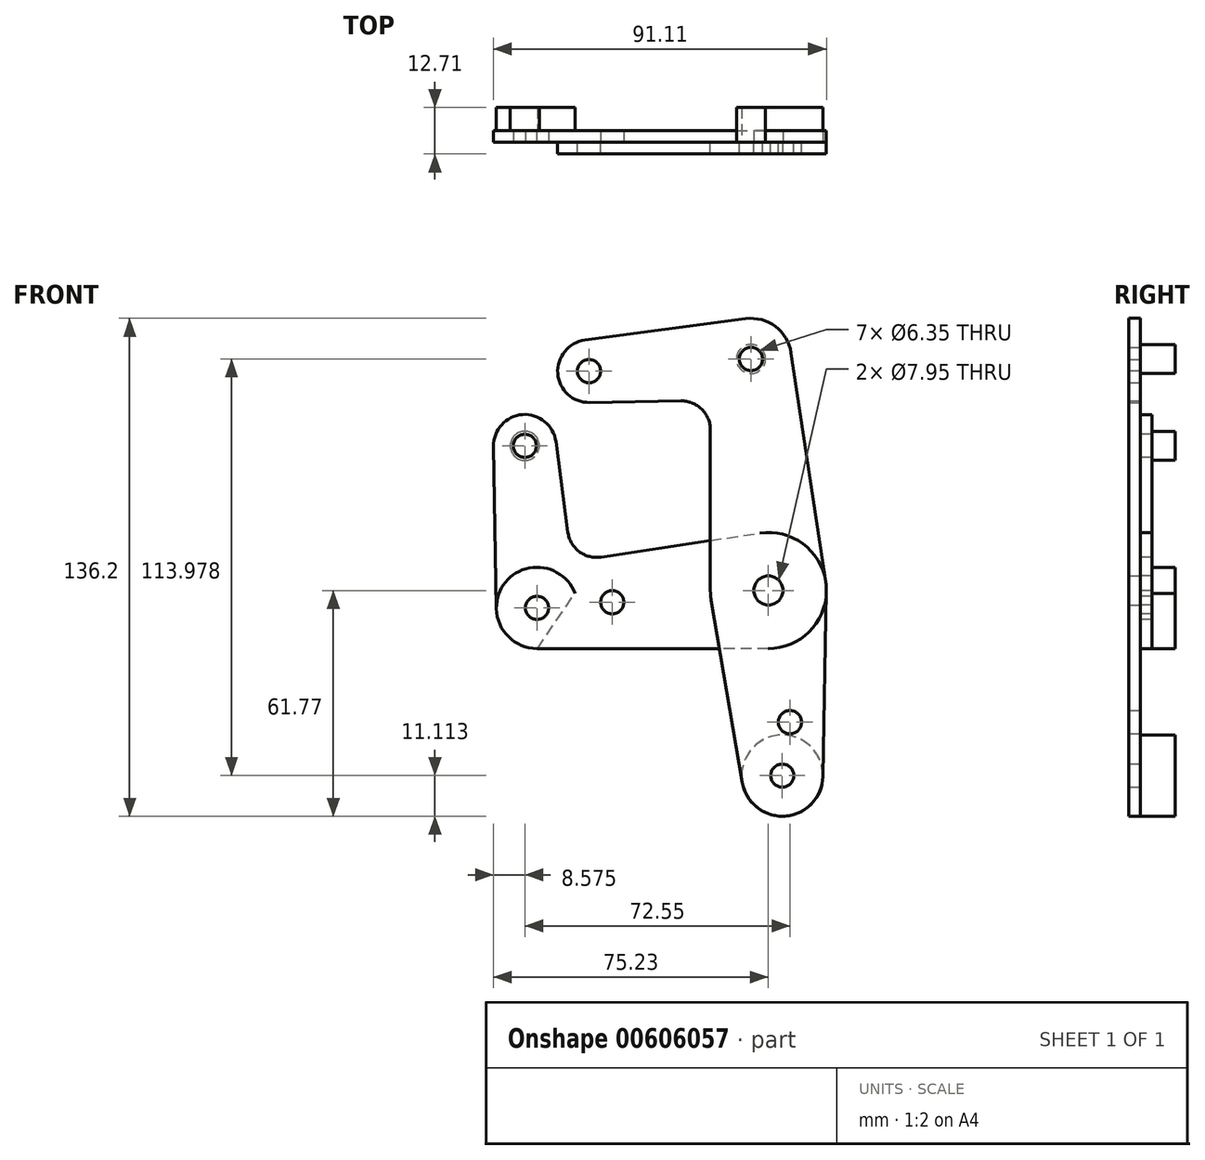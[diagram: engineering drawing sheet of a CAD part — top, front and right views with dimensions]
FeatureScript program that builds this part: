
annotation { "Feature Type Name" : "Feature", "Feature Type Description" : "" }
export const myFeature = defineFeature(function(context is Context, id is Id, definition is map)
    precondition{}
    {
        {
            var Q0;
            Q0=qCreatedBy(makeId("Front.planeOp"),FACE);
            var sketch = newSketch(context, id + "F0", { "sketchPlane" : qUnion([Q0])});
            skCircle(sketch, "E0", {"center": v(0, 0) * mm, "radius": 15.88 * mm});
            skCircle(sketch, "E1", {"center": v(0, 0) * mm, "radius": 3.98 * mm});
            skLineSegment(sketch, "E2", {"start": v(4.64, -61.74) * mm, "end": v(-4.76, 63.32) * mm, "construction": true});
            skLineSegment(sketch, "E3", {"start": v(-4.76, 63.32) * mm, "end": v(-49.09, 59.99) * mm, "construction": true});
            skCircle(sketch, "E4", {"center": v(-4.76, 63.32) * mm, "radius": 11.11 * mm});
            skCircle(sketch, "E5", {"center": v(-49.09, 59.99) * mm, "radius": 8.57 * mm});
            skCircle(sketch, "E6", {"center": v(3.81, -50.66) * mm, "radius": 11.11 * mm});
            skCircle(sketch, "E7", {"center": v(-4.76, 63.32) * mm, "radius": 3.18 * mm});
            skCircle(sketch, "E8", {"center": v(-49.09, 59.99) * mm, "radius": 3.18 * mm});
            skCircle(sketch, "E9", {"center": v(3.81, -50.66) * mm, "radius": 3.18 * mm});
            skLineSegment(sketch, "E10", {"start": v(0, 0) * mm, "end": v(-63.32, -4.76) * mm, "construction": true});
            skLineSegment(sketch, "E11", {"start": v(-63.32, -4.76) * mm, "end": v(-66.65, 39.56) * mm, "construction": true});
            skCircle(sketch, "E12", {"center": v(0, 0) * mm, "radius": 3.18 * mm});
            skLineSegment(sketch, "E13", {"start": v(6.22, 64.98) * mm, "end": v(15.7, 2.37) * mm});
            skLineSegment(sketch, "E14", {"start": v(15.87, -0.3) * mm, "end": v(14.92, -50.87) * mm});
            skLineSegment(sketch, "E15", {"start": v(-7.14, -52.53) * mm, "end": v(-15.65, -2.67) * mm});
            skLineSegment(sketch, "E16", {"start": v(-6.23, 74.34) * mm, "end": v(-50.22, 68.49) * mm});
            skCircle(sketch, "E17", {"center": v(-63.32, -4.76) * mm, "radius": 11.11 * mm});
            skCircle(sketch, "E18", {"center": v(-63.32, -4.76) * mm, "radius": 3.18 * mm});
            skCircle(sketch, "E19", {"center": v(-66.65, 39.56) * mm, "radius": 8.57 * mm});
            skCircle(sketch, "E20", {"center": v(-66.65, 39.56) * mm, "radius": 3.18 * mm});
            skCircle(sketch, "E21", {"center": v(-42.73, -3.21) * mm, "radius": 3.18 * mm});
            skCircle(sketch, "E22", {"center": v(5.9, -36.05) * mm, "radius": 3.18 * mm});
            skLineSegment(sketch, "E23", {"start": v(0, -15.88) * mm, "end": v(-63.32, -15.88) * mm});
            skLineSegment(sketch, "E24", {"start": v(-75.23, 39.4) * mm, "end": v(-74.43, -4.96) * mm});
            skLineSegment(sketch, "E25", {"start": v(-48.93, 51.42) * mm, "end": v(-23.97, 51.86) * mm});
            skLineSegment(sketch, "E26", {"start": v(-15.88, 0) * mm, "end": v(-15.87, 43.91) * mm});
            skArc(sketch, "E27.filletArc", {"start": v(-15.88, 43.91) * mm, "mid": v(-18.25, 49.59) * mm, "end": v(-23.97, 51.86) * mm});
            skLineSegment(sketch, "E28", {"start": v(5.9, -36.05) * mm, "end": v(2.75, -36.58) * mm, "construction": true});
            skLineSegment(sketch, "E29", {"start": v(-58.16, 40.7) * mm, "end": v(-54.86, 15.94) * mm});
            skLineSegment(sketch, "E30", {"start": v(-45.8, 9.13) * mm, "end": v(0, 16.06) * mm});
            skArc(sketch, "E31.filletArc", {"start": v(-54.86, 15.94) * mm, "mid": v(-51.76, 10.63) * mm, "end": v(-45.8, 9.13) * mm});
            skLineSegment(sketch, "E32", {"start": v(3.81, -50.66) * mm, "end": v(-63.32, -4.76) * mm, "construction": true});
            skSolve(sketch);
        }
        {
            var Q0;
            {var subQ0=sQuery(id+"F0.wireOp",EDGE,"E13");Q0=makeQuery(id+"F0.imprint","IMPRINT",FACE,{"disambiguationData":[TD([[makeQuery(id+"F0.imprint","IMPRINT",EDGE,{"derivedFrom":subQ0}),-1.0]])]});}
            var Q1;
            Q1=makeQuery(id+"F0.imprint","IMPRINT",FACE,{"disambiguationData":[TD([[makeQuery(id+"F0.imprint","IMPRINT",EDGE,{"derivedFrom":sQuery(id+"F0.wireOp",EDGE,"E1")}),-1.0]])]});
            var Q2;
            {var subQ0=sQuery(id+"F0.wireOp",EDGE,"E14");Q2=makeQuery(id+"F0.imprint","IMPRINT",FACE,{"disambiguationData":[TD([[makeQuery(id+"F0.imprint","IMPRINT",EDGE,{"derivedFrom":subQ0}),-1.0]])]});}
            var Q3;
            Q3=makeQuery(id+"F0.imprint","IMPRINT",FACE,{"disambiguationData":[TD([[makeQuery(id+"F0.imprint","IMPRINT",EDGE,{"derivedFrom":sQuery(id+"F0.wireOp",EDGE,"E9")}),-1.0]])]});
            var Q4;
            Q4=makeQuery(id+"F0.imprint","IMPRINT",FACE,{"disambiguationData":[TD([[makeQuery(id+"F0.imprint","IMPRINT",EDGE,{"derivedFrom":sQuery(id+"F0.wireOp",EDGE,"E7")}),-1.0]])]});
            var Q5;
            Q5=makeQuery(id+"F0.imprint","IMPRINT",FACE,{"disambiguationData":[TD([[makeQuery(id+"F0.imprint","IMPRINT",EDGE,{"derivedFrom":sQuery(id+"F0.wireOp",EDGE,"E8")}),-1.0]])]});
            var Q6;
            {var subQ0=sQuery(id+"F0.wireOp",EDGE,"E26");var subQ1=sQuery(id+"F0.wireOp",EDGE,"E0");var subQ2=makeQuery(id+"F0.imprint","INTERSECT",VERTEX,{"derivedFrom":[subQ1,subQ0]});Q6=makeQuery(id+"F0.imprint","IMPRINT",FACE,{"disambiguationData":[TD([[makeQuery(id+"F0.imprint","IMPRINT",EDGE,{"disambiguationData":[TD([[subQ2,1.0]])],"derivedFrom":subQ1}),-1.0]])]});}
            var Q7;
            {var subQ0=sQuery(id+"F0.wireOp",EDGE,"E15");var subQ1=sQuery(id+"F0.wireOp",EDGE,"E0");var subQ2=makeQuery(id+"F0.imprint","INTERSECT",VERTEX,{"derivedFrom":[subQ1,subQ0]});Q7=makeQuery(id+"F0.imprint","IMPRINT",FACE,{"disambiguationData":[TD([[makeQuery(id+"F0.imprint","IMPRINT",EDGE,{"disambiguationData":[TD([[subQ2,-1.0]])],"derivedFrom":subQ1}),-1.0]])]});}
            extrude(context, id + "F1", {"entities" : qUnion([Q0, Q1, Q2, Q3, Q4, Q5, Q6, Q7]), "depth" : 3.17 * mm, "offsetDistance" : 25.4 * mm});
        }
        {
            var Q0;
            Q0=makeQuery(id+"F0.imprint","IMPRINT",FACE,{"disambiguationData":[TD([[makeQuery(id+"F0.imprint","IMPRINT",EDGE,{"derivedFrom":sQuery(id+"F0.wireOp",EDGE,"E21")}),-1.0]])]});
            var Q1;
            Q1=makeQuery(id+"F0.imprint","IMPRINT",FACE,{"disambiguationData":[TD([[makeQuery(id+"F0.imprint","IMPRINT",EDGE,{"derivedFrom":sQuery(id+"F0.wireOp",EDGE,"E20")}),-1.0]])]});
            var Q2;
            Q2=makeQuery(id+"F0.imprint","IMPRINT",FACE,{"disambiguationData":[TD([[makeQuery(id+"F0.imprint","IMPRINT",EDGE,{"derivedFrom":sQuery(id+"F0.wireOp",EDGE,"E18")}),-1.0]])]});
            var Q3;
            {var subQ0=sQuery(id+"F0.wireOp",EDGE,"E26");var subQ1=sQuery(id+"F0.wireOp",EDGE,"E0");var subQ2=makeQuery(id+"F0.imprint","INTERSECT",VERTEX,{"derivedFrom":[subQ1,subQ0]});Q3=makeQuery(id+"F0.imprint","IMPRINT",FACE,{"disambiguationData":[TD([[makeQuery(id+"F0.imprint","IMPRINT",EDGE,{"disambiguationData":[TD([[subQ2,1.0]])],"derivedFrom":subQ1}),-1.0]])]});}
            var Q4;
            Q4=makeQuery(id+"F0.imprint","IMPRINT",FACE,{"disambiguationData":[TD([[makeQuery(id+"F0.imprint","IMPRINT",EDGE,{"derivedFrom":sQuery(id+"F0.wireOp",EDGE,"E1")}),-1.0]])]});
            var Q5;
            {var subQ0=sQuery(id+"F0.wireOp",EDGE,"E15");var subQ1=sQuery(id+"F0.wireOp",EDGE,"E0");var subQ2=makeQuery(id+"F0.imprint","INTERSECT",VERTEX,{"derivedFrom":[subQ1,subQ0]});Q5=makeQuery(id+"F0.imprint","IMPRINT",FACE,{"disambiguationData":[TD([[makeQuery(id+"F0.imprint","IMPRINT",EDGE,{"disambiguationData":[TD([[subQ2,-1.0]])],"derivedFrom":subQ1}),-1.0]])]});}
            extrude(context, id + "F2", {"entities" : qUnion([Q0, Q1, Q2, Q3, Q4, Q5]), "oppositeDirection" : true, "depth" : 3.17 * mm, "offsetDistance" : 25.4 * mm});
        }
        {
            var Q0;
            Q0=makeQuery(id+"F1.opExtrude","CAP_FACE",FACE,{"disambiguationData":[OSD([sQuery(id+"F0.wireOp",EDGE,"E0"),sQuery(id+"F0.wireOp",EDGE,"E1"),sQuery(id+"F0.wireOp",EDGE,"E4"),sQuery(id+"F0.wireOp",EDGE,"E5"),sQuery(id+"F0.wireOp",EDGE,"E6"),sQuery(id+"F0.wireOp",EDGE,"E7"),sQuery(id+"F0.wireOp",EDGE,"E8"),sQuery(id+"F0.wireOp",EDGE,"E9"),sQuery(id+"F0.wireOp",EDGE,"E13"),sQuery(id+"F0.wireOp",EDGE,"E14"),sQuery(id+"F0.wireOp",EDGE,"E15"),sQuery(id+"F0.wireOp",EDGE,"E16"),sQuery(id+"F0.wireOp",EDGE,"E22"),sQuery(id+"F0.wireOp",EDGE,"E25"),sQuery(id+"F0.wireOp",EDGE,"E26"),sQuery(id+"F0.wireOp",EDGE,"E27.filletArc")])],"isStart":false});
            var sketch = newSketch(context, id + "F3", { "sketchPlane" : qUnion([Q0])});
            skCircle(sketch, "E33", {"center": v(-4.76, 63.32) * mm, "radius": 3.98 * mm});
            skCircle(sketch, "E34", {"center": v(0, 0) * mm, "radius": 3.98 * mm});
            skCircle(sketch, "E35", {"center": v(3.81, -50.66) * mm, "radius": 11.11 * mm});
            skSolve(sketch);
        }
        {
            var Q0;
            Q0=makeQuery(id+"F2.opExtrude","CAP_FACE",FACE,{"disambiguationData":[OSD([sQuery(id+"F0.wireOp",EDGE,"E0"),sQuery(id+"F0.wireOp",EDGE,"E1"),sQuery(id+"F0.wireOp",EDGE,"E17"),sQuery(id+"F0.wireOp",EDGE,"E18"),sQuery(id+"F0.wireOp",EDGE,"E19"),sQuery(id+"F0.wireOp",EDGE,"E20"),sQuery(id+"F0.wireOp",EDGE,"E21"),sQuery(id+"F0.wireOp",EDGE,"E23"),sQuery(id+"F0.wireOp",EDGE,"E24"),sQuery(id+"F0.wireOp",EDGE,"E29"),sQuery(id+"F0.wireOp",EDGE,"E30"),sQuery(id+"F0.wireOp",EDGE,"E31.filletArc")])],"isStart":false});
            var sketch = newSketch(context, id + "F4", { "sketchPlane" : qUnion([Q0])});
            skCircle(sketch, "E36", {"center": v(63.32, -4.76) * mm, "radius": 11.11 * mm});
            skCircle(sketch, "E37", {"center": v(66.65, 39.56) * mm, "radius": 3.98 * mm});
            skLineSegment(sketch, "E38", {"start": v(52.93, -0.82) * mm, "end": v(63.23, -15.87) * mm});
            skSolve(sketch);
        }
        {
            var Q0;
            Q0=qCreatedBy(makeId("Front.planeOp"),FACE);
            cPlane(context, id + "F5", {"entities" : qUnion([Q0]), "cplaneType" : CPlaneType.OFFSET, "offset" : 9.52 * mm, "oppositeDirection" : true, "width" : 152.4 * mm, "height" : 152.4 * mm});
        }
        {
            var Q0;
            Q0=makeQuery(id+"F3.imprint","IMPRINT",FACE,{"disambiguationData":[TD([[makeQuery(id+"F3.imprint","IMPRINT",EDGE,{"derivedFrom":makeQuery(id+"F1.opExtrude","CAP_EDGE",EDGE,{"disambiguationData":[OSD([sQuery(id+"F0.wireOp",EDGE,"E9")])],"isStart":false})}),-1.0]])]});
            var Q1;
            Q1=makeQuery(id+"F3.imprint","IMPRINT",FACE,{"disambiguationData":[TD([[makeQuery(id+"F3.imprint","IMPRINT",EDGE,{"derivedFrom":makeQuery(id+"F1.opExtrude","CAP_EDGE",EDGE,{"disambiguationData":[OSD([sQuery(id+"F0.wireOp",EDGE,"E9")])],"isStart":false})}),1.0]])]});
            var Q2;
            Q2=sQuery(id+"F3.wireOp",EDGE,"E35");
            var Q3;
            Q3=qCreatedBy(id+"F5.planeOp",FACE);
            extrude(context, id + "F6", {"entities" : qUnion([Q0, Q1]), "surfaceEntities" : qUnion([Q2]), "endBound" : BoundingType.UP_TO_SURFACE, "oppositeDirection" : true, "depth" : 25.4 * mm, "endBoundEntityFace" : qUnion([Q3]), "offsetDistance" : 25.4 * mm});
        }
        {
            var Q0;
            Q0=makeQuery(id+"F3.imprint","IMPRINT",FACE,{"disambiguationData":[TD([[makeQuery(id+"F3.imprint","IMPRINT",EDGE,{"derivedFrom":sQuery(id+"F3.wireOp",EDGE,"E33")}),1.0]])]});
            var Q1;
            Q1=makeQuery(id+"F3.imprint","IMPRINT",FACE,{"disambiguationData":[TD([[makeQuery(id+"F3.imprint","IMPRINT",EDGE,{"derivedFrom":makeQuery(id+"F1.opExtrude","CAP_EDGE",EDGE,{"disambiguationData":[OSD([sQuery(id+"F0.wireOp",EDGE,"E7")])],"isStart":false})}),1.0]])]});
            var Q2;
            Q2=qCreatedBy(id+"F5.planeOp",FACE);
            extrude(context, id + "F7", {"entities" : qUnion([Q0, Q1]), "endBound" : BoundingType.UP_TO_SURFACE, "oppositeDirection" : true, "depth" : 25.4 * mm, "endBoundEntityFace" : qUnion([Q2]), "offsetDistance" : 25.4 * mm});
        }
        {
            var Q0;
            Q0=makeQuery(id+"F4.imprint","IMPRINT",FACE,{"disambiguationData":[TD([[makeQuery(id+"F4.imprint","IMPRINT",EDGE,{"derivedFrom":sQuery(id+"F4.wireOp",EDGE,"E37")}),1.0]])]});
            var Q1;
            Q1=makeQuery(id+"F4.imprint","IMPRINT",FACE,{"disambiguationData":[TD([[makeQuery(id+"F4.imprint","IMPRINT",EDGE,{"derivedFrom":makeQuery(id+"F2.opExtrude","CAP_EDGE",EDGE,{"disambiguationData":[OSD([sQuery(id+"F0.wireOp",EDGE,"E20")])],"isStart":false})}),-1.0]])]});
            var Q2;
            Q2=qCreatedBy(id+"F5.planeOp",FACE);
            extrude(context, id + "F8", {"entities" : qUnion([Q0, Q1]), "endBound" : BoundingType.UP_TO_SURFACE, "depth" : 25.4 * mm, "endBoundEntityFace" : qUnion([Q2]), "offsetDistance" : 25.4 * mm});
        }
        {
            var Q0;
            {var subQ0=sQuery(id+"F4.wireOp",EDGE,"E38");Q0=makeQuery(id+"F4.imprint","IMPRINT",FACE,{"disambiguationData":[TD([[makeQuery(id+"F4.imprint","IMPRINT",EDGE,{"derivedFrom":subQ0}),1.0]])]});}
            var Q1;
            Q1=makeQuery(id+"F4.imprint","IMPRINT",FACE,{"disambiguationData":[TD([[makeQuery(id+"F4.imprint","IMPRINT",EDGE,{"derivedFrom":makeQuery(id+"F2.opExtrude","CAP_EDGE",EDGE,{"disambiguationData":[OSD([sQuery(id+"F0.wireOp",EDGE,"E18")])],"isStart":false})}),-1.0]])]});
            var Q2;
            Q2=qCreatedBy(id+"F5.planeOp",FACE);
            extrude(context, id + "F9", {"entities" : qUnion([Q0, Q1]), "endBound" : BoundingType.UP_TO_SURFACE, "depth" : 25.4 * mm, "endBoundEntityFace" : qUnion([Q2]), "offsetDistance" : 25.4 * mm});
        }
        {
            var Q0;
            Q0=makeQuery(id+"F1.opExtrude","SWEPT_BODY",BODY,{"disambiguationData":[OSD([sQuery(id+"F0.wireOp",EDGE,"E0"),sQuery(id+"F0.wireOp",EDGE,"E1"),sQuery(id+"F0.wireOp",EDGE,"E4"),sQuery(id+"F0.wireOp",EDGE,"E5"),sQuery(id+"F0.wireOp",EDGE,"E6"),sQuery(id+"F0.wireOp",EDGE,"E7"),sQuery(id+"F0.wireOp",EDGE,"E8"),sQuery(id+"F0.wireOp",EDGE,"E9"),sQuery(id+"F0.wireOp",EDGE,"E13"),sQuery(id+"F0.wireOp",EDGE,"E14"),sQuery(id+"F0.wireOp",EDGE,"E15"),sQuery(id+"F0.wireOp",EDGE,"E16"),sQuery(id+"F0.wireOp",EDGE,"E22"),sQuery(id+"F0.wireOp",EDGE,"E25"),sQuery(id+"F0.wireOp",EDGE,"E26"),sQuery(id+"F0.wireOp",EDGE,"E27.filletArc")])]});
            var Q1;
            Q1=makeQuery(id+"F7.opExtrude","SWEPT_BODY",BODY,{"disambiguationData":[OSD([sQuery(id+"F3.wireOp",EDGE,"E33")])]});
            var Q2;
            Q2=makeQuery(id+"F6.opExtrude","SWEPT_BODY",BODY,{"disambiguationData":[OSD([sQuery(id+"F3.wireOp",EDGE,"E35")])]});
            booleanBodies(context, id + "F10", {"operationType" : BooleanOperationType.SUBTRACTION, "tools" : qUnion([Q0]), "targets" : qUnion([Q1, Q2]), "keepTools" : true});
        }
        {
            var Q0;
            Q0=makeQuery(id+"F2.opExtrude","SWEPT_BODY",BODY,{"disambiguationData":[OSD([sQuery(id+"F0.wireOp",EDGE,"E0"),sQuery(id+"F0.wireOp",EDGE,"E1"),sQuery(id+"F0.wireOp",EDGE,"E17"),sQuery(id+"F0.wireOp",EDGE,"E18"),sQuery(id+"F0.wireOp",EDGE,"E19"),sQuery(id+"F0.wireOp",EDGE,"E20"),sQuery(id+"F0.wireOp",EDGE,"E21"),sQuery(id+"F0.wireOp",EDGE,"E23"),sQuery(id+"F0.wireOp",EDGE,"E24"),sQuery(id+"F0.wireOp",EDGE,"E29"),sQuery(id+"F0.wireOp",EDGE,"E30"),sQuery(id+"F0.wireOp",EDGE,"E31.filletArc")])]});
            var Q1;
            Q1=makeQuery(id+"F8.opExtrude","SWEPT_BODY",BODY,{"disambiguationData":[OSD([sQuery(id+"F4.wireOp",EDGE,"E37")])]});
            var Q2;
            Q2=makeQuery(id+"F9.opExtrude","SWEPT_BODY",BODY,{"disambiguationData":[OSD([sQuery(id+"F4.wireOp",EDGE,"E36"),sQuery(id+"F4.wireOp",EDGE,"E38")])]});
            booleanBodies(context, id + "F11", {"operationType" : BooleanOperationType.SUBTRACTION, "tools" : qUnion([Q0]), "targets" : qUnion([Q1, Q2]), "keepTools" : true});
        }
    });
